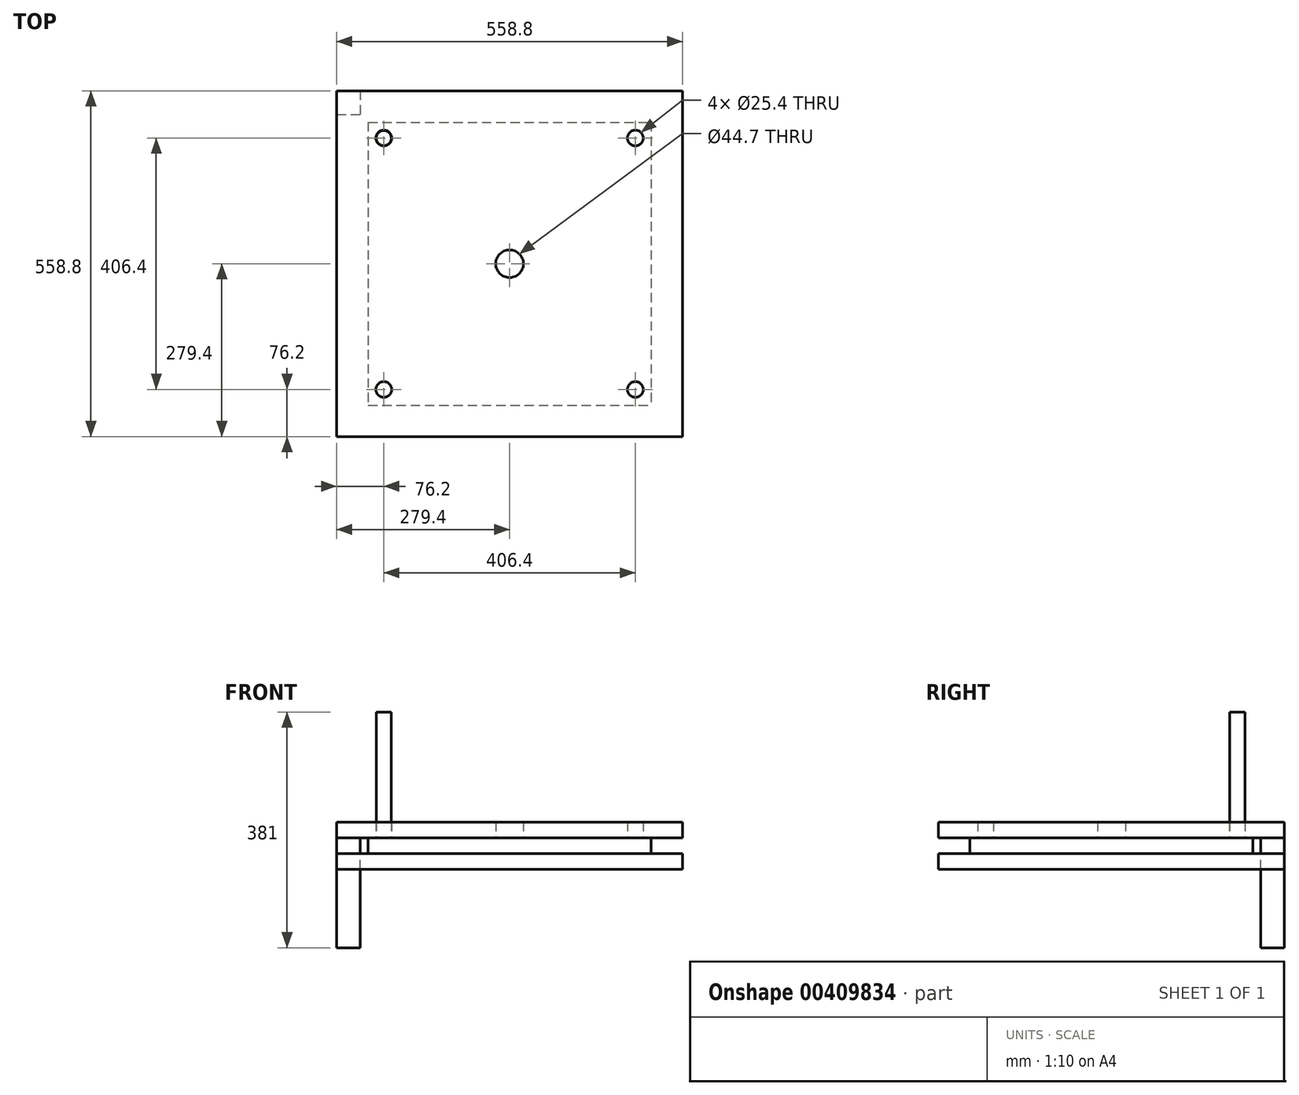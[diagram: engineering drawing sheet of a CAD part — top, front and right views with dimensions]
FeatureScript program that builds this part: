
annotation { "Feature Type Name" : "Feature", "Feature Type Description" : "" }
export const myFeature = defineFeature(function(context is Context, id is Id, definition is map)
    precondition{}
    {
        {
            var Q0;
            Q0=qCreatedBy(makeId("Top.planeOp"),FACE);
            var sketch = newSketch(context, id + "F0", { "sketchPlane" : qUnion([Q0])});
            skLineSegment(sketch, "E0.bottom", {"start": v(-279.4, 279.4) * mm, "end": v(279.4, 279.4) * mm});
            skLineSegment(sketch, "E0.top", {"start": v(-279.4, -279.4) * mm, "end": v(279.4, -279.4) * mm});
            skLineSegment(sketch, "E0.left", {"start": v(-279.4, 279.4) * mm, "end": v(-279.4, -279.4) * mm});
            skLineSegment(sketch, "E0.right", {"start": v(279.4, 279.4) * mm, "end": v(279.4, -279.4) * mm});
            skLineSegment(sketch, "E1.0", {"start": v(-228.6, 228.6) * mm, "end": v(-228.6, -228.6) * mm, "construction": true});
            skLineSegment(sketch, "E1.1", {"start": v(-228.6, 228.6) * mm, "end": v(228.6, 228.6) * mm, "construction": true});
            skLineSegment(sketch, "E1.2", {"start": v(228.6, 228.6) * mm, "end": v(228.6, -228.6) * mm, "construction": true});
            skLineSegment(sketch, "E1.3", {"start": v(-228.6, -228.6) * mm, "end": v(228.6, -228.6) * mm, "construction": true});
            skCircle(sketch, "E2", {"center": v(0, 0) * mm, "radius": 22.35 * mm});
            skLineSegment(sketch, "E3.0", {"start": v(-203.2, 203.2) * mm, "end": v(203.2, 203.2) * mm, "construction": true});
            skLineSegment(sketch, "E3.1", {"start": v(-203.2, 203.2) * mm, "end": v(-203.2, -203.2) * mm, "construction": true});
            skLineSegment(sketch, "E3.2", {"start": v(-203.2, -203.2) * mm, "end": v(203.2, -203.2) * mm, "construction": true});
            skLineSegment(sketch, "E3.3", {"start": v(203.2, 203.2) * mm, "end": v(203.2, -203.2) * mm, "construction": true});
            skCircle(sketch, "E4", {"center": v(-203.2, 203.2) * mm, "radius": 12.7 * mm});
            skCircle(sketch, "E5", {"center": v(203.2, 203.2) * mm, "radius": 12.7 * mm});
            skCircle(sketch, "E6", {"center": v(203.2, -203.2) * mm, "radius": 12.7 * mm});
            skCircle(sketch, "E7", {"center": v(-203.2, -203.2) * mm, "radius": 12.7 * mm});
            skSolve(sketch);
        }
        {
            var Q0;
            Q0 = qSketchRegion(id + "F0", true);
            extrude(context, id + "F1", {"entities" : qUnion([Q0]), "depth" : 25.4 * mm});
        }
        {
            var Q0;
            Q0=qCreatedBy(makeId("Top.planeOp"),FACE);
            var sketch = newSketch(context, id + "F2", { "sketchPlane" : qUnion([Q0])});
            skLineSegment(sketch, "E8.0", {"start": v(-228.6, 228.6) * mm, "end": v(-228.6, -228.6) * mm});
            skLineSegment(sketch, "E8.1", {"start": v(-228.6, 228.6) * mm, "end": v(228.6, 228.6) * mm});
            skLineSegment(sketch, "E8.2", {"start": v(228.6, 228.6) * mm, "end": v(228.6, -228.6) * mm});
            skLineSegment(sketch, "E8.3", {"start": v(-228.6, -228.6) * mm, "end": v(228.6, -228.6) * mm});
            skSolve(sketch);
        }
        {
            var Q0;
            Q0 = qSketchRegion(id + "F2", true);
            extrude(context, id + "F3", {"entities" : qUnion([Q0]), "oppositeDirection" : true, "depth" : 25.4 * mm});
        }
        {
            var Q0;
            Q0=qCreatedBy(makeId("Top.planeOp"),FACE);
            var sketch = newSketch(context, id + "F4", { "sketchPlane" : qUnion([Q0])});
            skLineSegment(sketch, "E9.0", {"start": v(-279.4, 279.4) * mm, "end": v(279.4, 279.4) * mm, "construction": true});
            skLineSegment(sketch, "E9.1", {"start": v(-279.4, 279.4) * mm, "end": v(-279.4, -279.4) * mm, "construction": true});
            skLineSegment(sketch, "E9.2", {"start": v(-279.4, -279.4) * mm, "end": v(279.4, -279.4) * mm, "construction": true});
            skLineSegment(sketch, "E9.3", {"start": v(279.4, 279.4) * mm, "end": v(279.4, -279.4) * mm, "construction": true});
            skLineSegment(sketch, "E10.bottom", {"start": v(-279.4, 279.4) * mm, "end": v(-241.3, 279.4) * mm});
            skLineSegment(sketch, "E10.top", {"start": v(-279.4, 241.3) * mm, "end": v(-241.3, 241.3) * mm});
            skLineSegment(sketch, "E10.left", {"start": v(-279.4, 279.4) * mm, "end": v(-279.4, 241.3) * mm});
            skLineSegment(sketch, "E10.right", {"start": v(-241.3, 279.4) * mm, "end": v(-241.3, 241.3) * mm});
            skSolve(sketch);
        }
        {
            var Q0;
            Q0 = qSketchRegion(id + "F4", true);
            extrude(context, id + "F5", {"entities" : qUnion([Q0]), "oppositeDirection" : true, "depth" : 177.8 * mm});
        }
        {
            var Q0;
            Q0=makeQuery(id+"F3.opExtrude","CAP_FACE",FACE,{"disambiguationData":[OSD([sQuery(id+"F2.wireOp",EDGE,"E8.0"),sQuery(id+"F2.wireOp",EDGE,"E8.1"),sQuery(id+"F2.wireOp",EDGE,"E8.2"),sQuery(id+"F2.wireOp",EDGE,"E8.3")])],"isStart":false});
            var sketch = newSketch(context, id + "F6", { "sketchPlane" : qUnion([Q0])});
            skLineSegment(sketch, "E11.0", {"start": v(-279.4, 279.4) * mm, "end": v(279.4, 279.4) * mm});
            skLineSegment(sketch, "E11.1", {"start": v(-279.4, -279.4) * mm, "end": v(-279.4, 279.4) * mm});
            skLineSegment(sketch, "E11.2", {"start": v(-279.4, -279.4) * mm, "end": v(279.4, -279.4) * mm});
            skLineSegment(sketch, "E11.3", {"start": v(279.4, -279.4) * mm, "end": v(279.4, 279.4) * mm});
            skSolve(sketch);
        }
        {
            var Q0;
            Q0 = qSketchRegion(id + "F6", true);
            extrude(context, id + "F7", {"entities" : qUnion([Q0]), "depth" : 25.4 * mm});
        }
        {
            var Q0;
            Q0=makeQuery(id+"F0.imprint","IMPRINT",FACE,{"disambiguationData":[TD([[makeQuery(id+"F0.imprint","IMPRINT",EDGE,{"derivedFrom":sQuery(id+"F0.wireOp",EDGE,"E4")}),1.0]])]});
            var sketch = newSketch(context, id + "F8", { "sketchPlane" : qUnion([Q0])});
            skCircle(sketch, "E12.0", {"center": v(-203.2, 203.2) * mm, "radius": 12.2 * mm});
            skSolve(sketch);
        }
        {
            var Q0;
            Q0=makeQuery(id+"F8.imprint","IMPRINT",FACE,{"disambiguationData":[TD([[makeQuery(id+"F8.imprint","IMPRINT",EDGE,{"derivedFrom":sQuery(id+"F8.wireOp",EDGE,"E12.0")}),1.0]])]});
            extrude(context, id + "F9", {"entities" : qUnion([Q0]), "depth" : 203.2 * mm});
        }
    });
